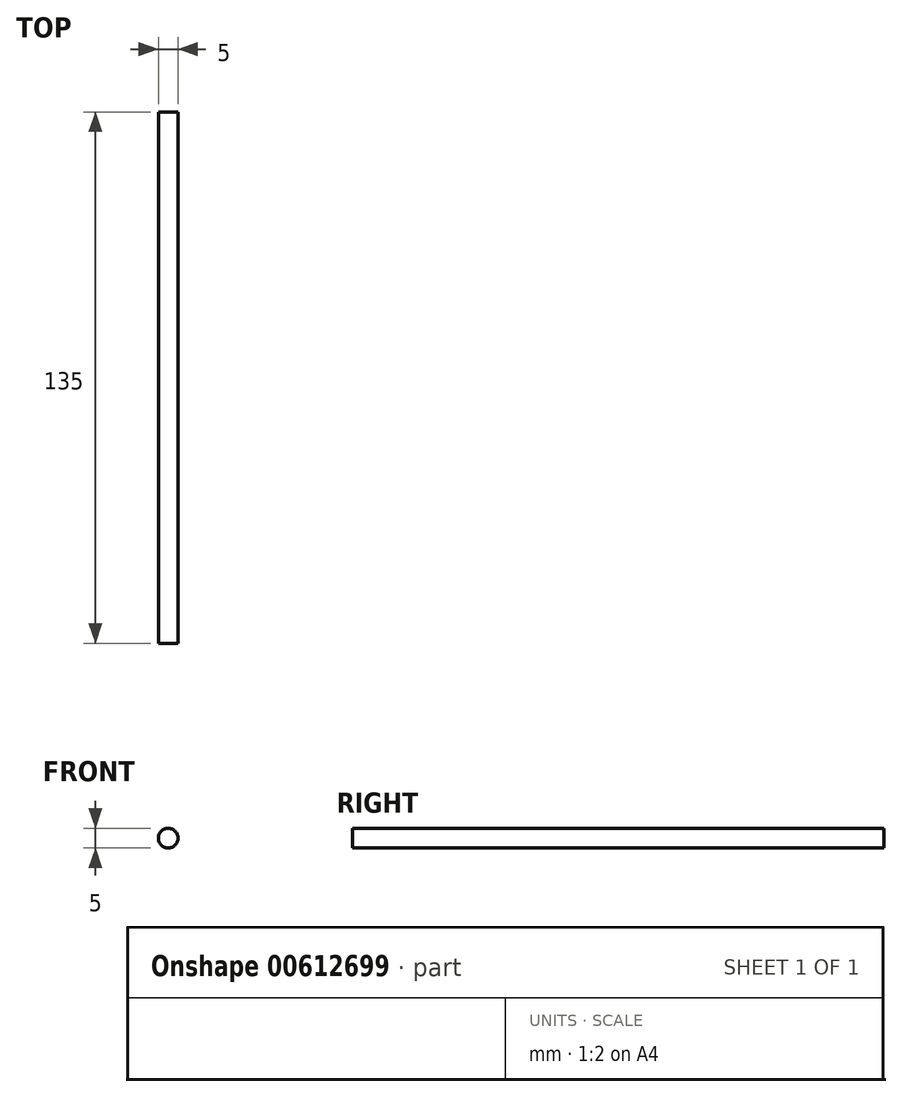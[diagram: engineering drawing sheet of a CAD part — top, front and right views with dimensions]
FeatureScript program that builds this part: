
annotation { "Feature Type Name" : "Feature", "Feature Type Description" : "" }
export const myFeature = defineFeature(function(context is Context, id is Id, definition is map)
    precondition{}
    {
        {
            var Q0;
            Q0=qCreatedBy(makeId("Front.planeOp"),FACE);
            var sketch = newSketch(context, id + "F0", { "sketchPlane" : qUnion([Q0])});
            skCircle(sketch, "E0", {"center": v(0, 0) * mm, "radius": 2.5 * mm});
            skSolve(sketch);
        }
        {
            var Q0;
            Q0=makeQuery(id+"F0.imprint","IMPRINT",FACE,{"disambiguationData":[TD([[makeQuery(id+"F0.imprint","IMPRINT",EDGE,{"derivedFrom":sQuery(id+"F0.wireOp",EDGE,"E0")}),1.0]])]});
            extrude(context, id + "F1", {"entities" : qUnion([Q0]), "endBound" : BoundingType.SYMMETRIC, "depth" : 135 * mm, "offsetDistance" : 25 * mm});
        }
    });
